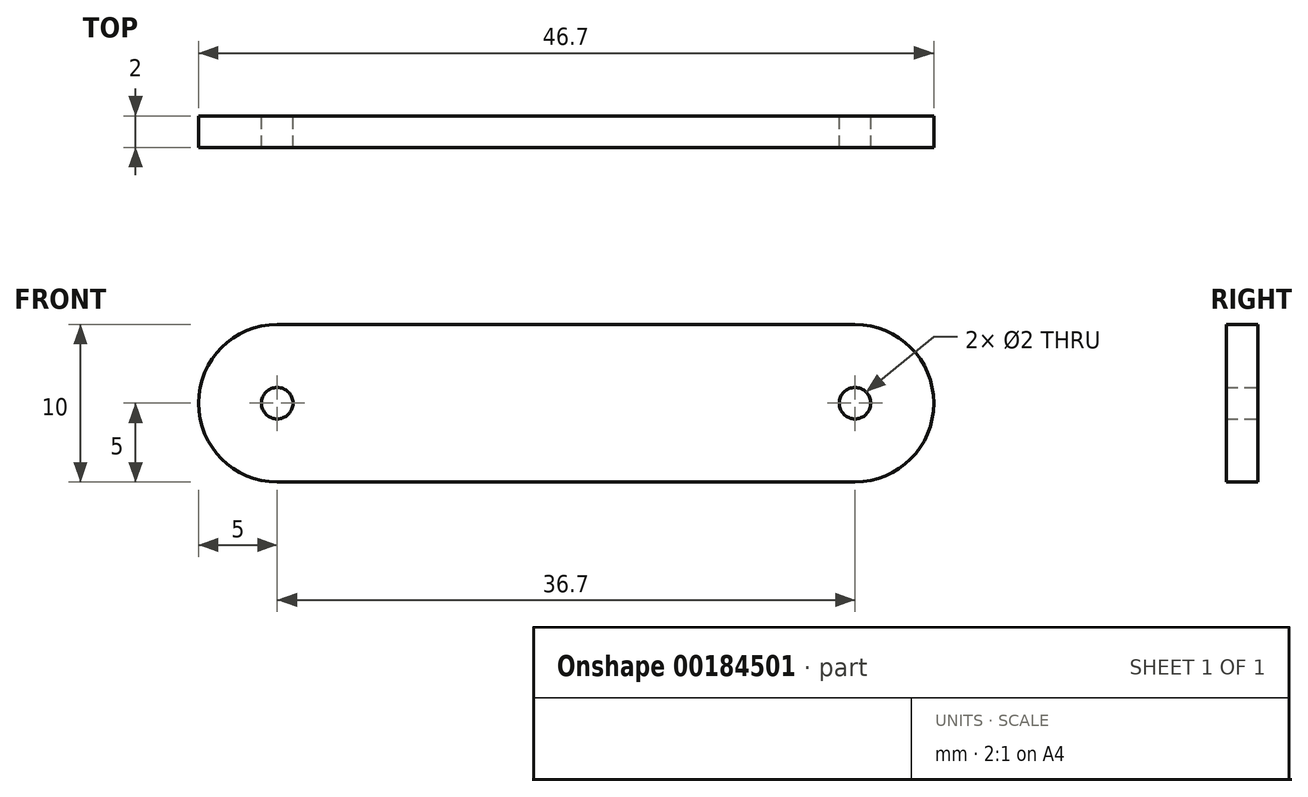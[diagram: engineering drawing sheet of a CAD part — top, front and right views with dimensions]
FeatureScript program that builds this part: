
annotation { "Feature Type Name" : "Feature", "Feature Type Description" : "" }
export const myFeature = defineFeature(function(context is Context, id is Id, definition is map)
    precondition{}
    {
        {
            var Q0;
            Q0=qCreatedBy(makeId("Front.planeOp"),FACE);
            var sketch = newSketch(context, id + "F0", { "sketchPlane" : qUnion([Q0])});
            skLineSegment(sketch, "E0.bottom", {"start": v(0, 0) * mm, "end": v(46.7, 0) * mm});
            skLineSegment(sketch, "E0.top", {"start": v(0, -10) * mm, "end": v(46.7, -10) * mm});
            skLineSegment(sketch, "E0.left", {"start": v(0, 0) * mm, "end": v(0, -10) * mm});
            skLineSegment(sketch, "E0.right", {"start": v(46.7, 0) * mm, "end": v(46.7, -10) * mm});
            skCircle(sketch, "E1", {"center": v(5, -5) * mm, "radius": 1 * mm});
            skCircle(sketch, "E2", {"center": v(41.7, -5) * mm, "radius": 1 * mm});
            skSolve(sketch);
        }
        {
            var Q0;
            Q0=makeQuery(id+"F0.imprint","IMPRINT",FACE,{"disambiguationData":[TD([[makeQuery(id+"F0.imprint","IMPRINT",EDGE,{"derivedFrom":sQuery(id+"F0.wireOp",EDGE,"E0.bottom")}),-1.0]])]});
            extrude(context, id + "F1", {"entities" : qUnion([Q0]), "depth" : 2 * mm});
        }
        {
            var Q0;
            Q0=makeQuery(id+"F1.opExtrude","SWEPT_EDGE",EDGE,{"disambiguationData":[OSD([sQuery(id+"F0.wireOp",EDGE,"E0.bottom"),sQuery(id+"F0.wireOp",EDGE,"E0.left")])]});
            var Q1;
            Q1=makeQuery(id+"F1.opExtrude","SWEPT_EDGE",EDGE,{"disambiguationData":[OSD([sQuery(id+"F0.wireOp",EDGE,"E0.top"),sQuery(id+"F0.wireOp",EDGE,"E0.left")])]});
            var Q2;
            Q2=makeQuery(id+"F1.opExtrude","SWEPT_EDGE",EDGE,{"disambiguationData":[OSD([sQuery(id+"F0.wireOp",EDGE,"E0.bottom"),sQuery(id+"F0.wireOp",EDGE,"E0.right")])]});
            var Q3;
            Q3=makeQuery(id+"F1.opExtrude","SWEPT_EDGE",EDGE,{"disambiguationData":[OSD([sQuery(id+"F0.wireOp",EDGE,"E0.top"),sQuery(id+"F0.wireOp",EDGE,"E0.right")])]});
            fillet(context, id + "F2", {"entities" : qUnion([Q0, Q1, Q2, Q3]), "radius" : 5 * mm, "tangentPropagation" : true, "allowEdgeOverflow" : false});
        }
    });
